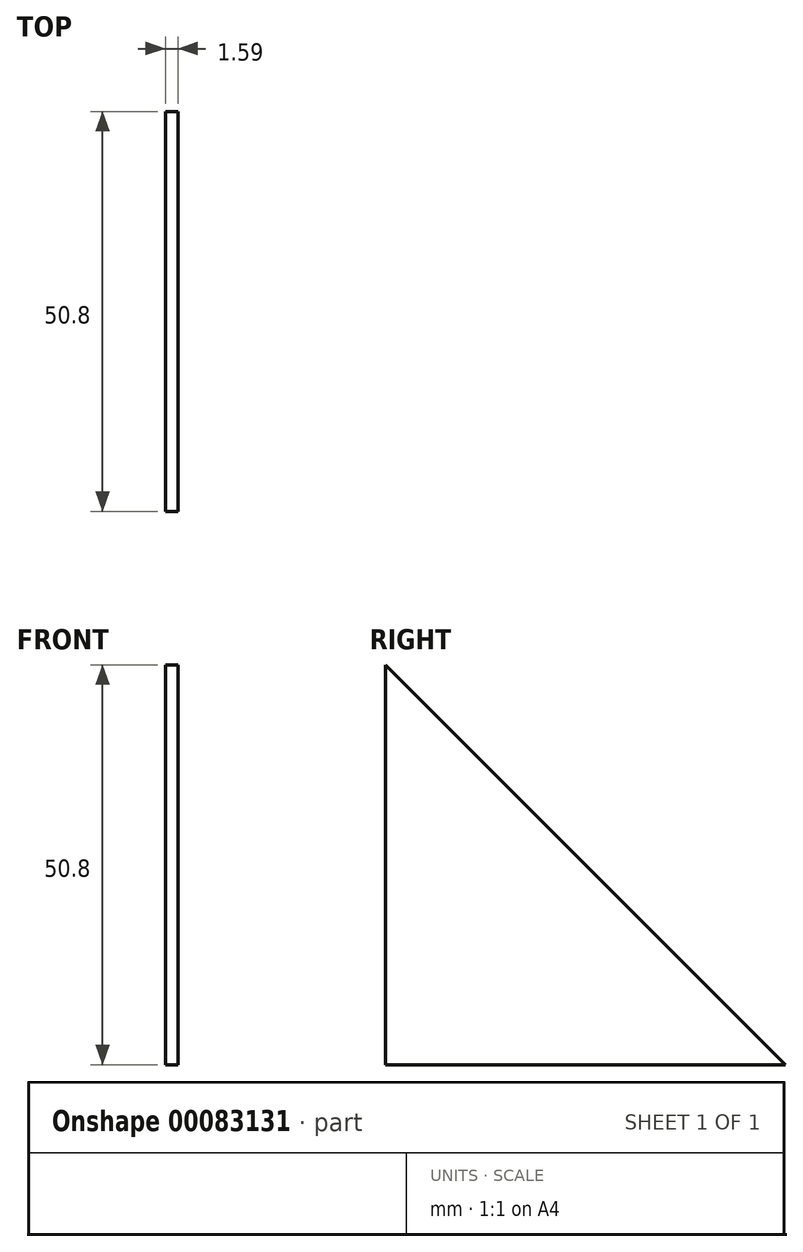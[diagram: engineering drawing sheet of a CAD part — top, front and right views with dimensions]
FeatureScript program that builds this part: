
annotation { "Feature Type Name" : "Feature", "Feature Type Description" : "" }
export const myFeature = defineFeature(function(context is Context, id is Id, definition is map)
    precondition{}
    {
        {
            var Q0;
            Q0=qCreatedBy(makeId("Right.planeOp"),FACE);
            var sketch = newSketch(context, id + "F0", { "sketchPlane" : qUnion([Q0])});
            skLineSegment(sketch, "E0", {"start": v(0, 0) * mm, "end": v(0, 50.8) * mm});
            skLineSegment(sketch, "E1", {"start": v(0, 50.8) * mm, "end": v(50.8, 0) * mm});
            skLineSegment(sketch, "E2", {"start": v(50.8, 0) * mm, "end": v(0, 0) * mm});
            skSolve(sketch);
        }
        {
            var Q0;
            Q0=makeQuery(id+"F0.imprint","IMPRINT",FACE,{"disambiguationData":[TD([[makeQuery(id+"F0.imprint","IMPRINT",EDGE,{"derivedFrom":sQuery(id+"F0.wireOp",EDGE,"E0")}),-1.0]])]});
            extrude(context, id + "F1", {"entities" : qUnion([Q0]), "depth" : 1.59 * mm});
        }
    });
